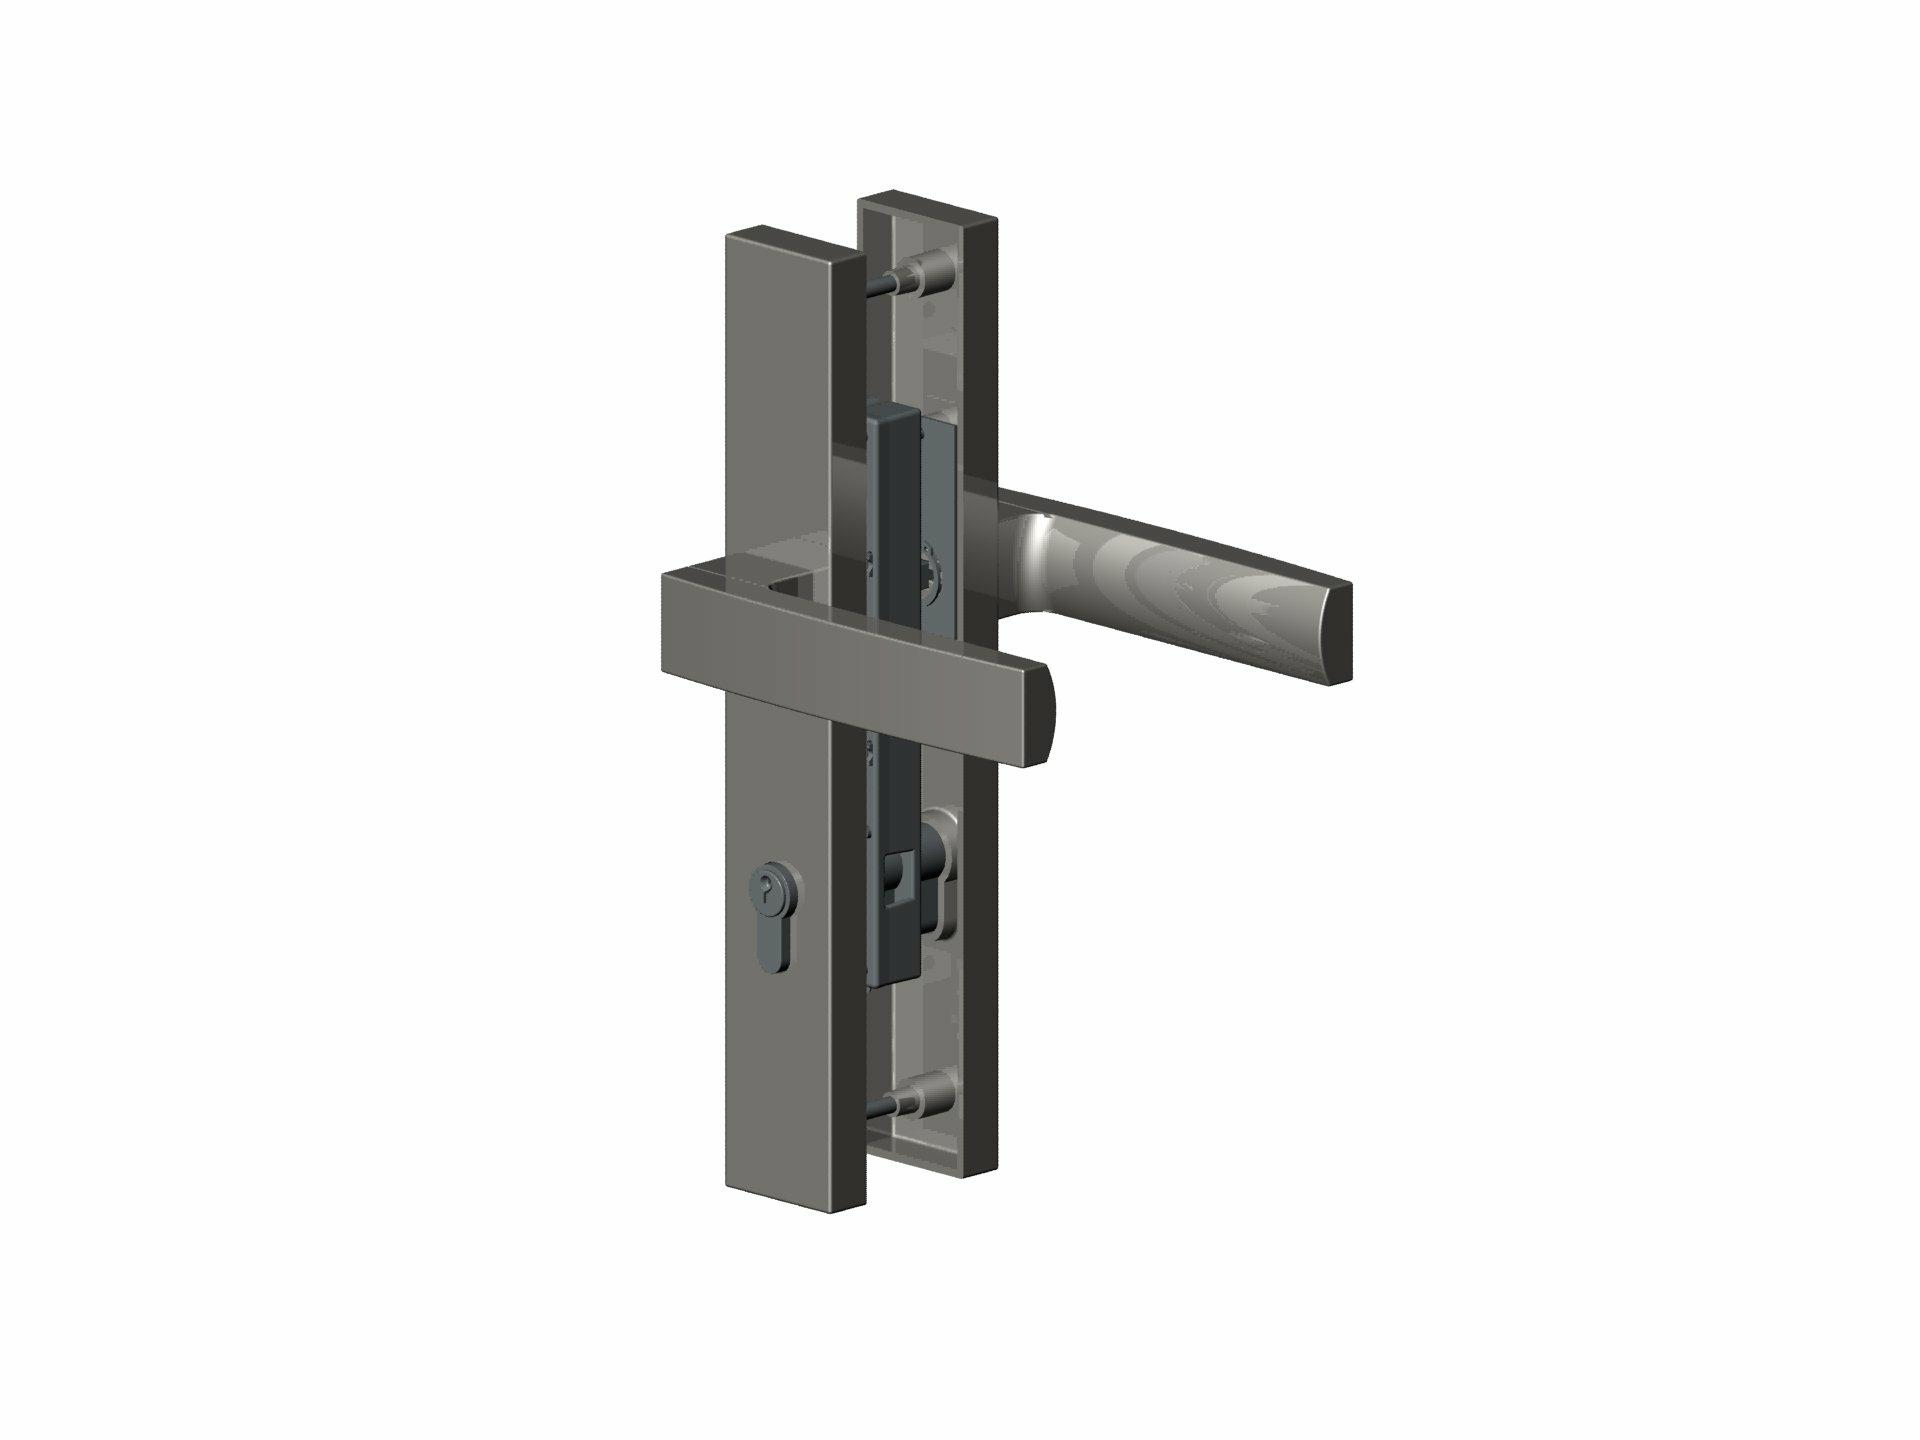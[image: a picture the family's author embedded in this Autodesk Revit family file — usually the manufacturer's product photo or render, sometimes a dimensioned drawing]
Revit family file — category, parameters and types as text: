
# Revit family: APL Magnum 50 French Door
name_source: partatom
category: Doors
revit_build: Autodesk Revit LT 2018 (Build: 20170223_1515(x64)
units: mm (PartAtom-declared; Revit-internal decimal feet)

## family parameters
Always vertical = Yes
Cut with Voids When Loaded = No
Host = Wall
OmniClass Number = 23.30.10.00
OmniClass Title = Doors
Room Calculation Point = No
Shared = No

## types (2) — shared parameters
15° Opening = Yes
90° Opening = No
Analytic Construction = <None>
Architrave = Yes
Frame Projection Ext. = 13 mm
Frame Projection Int. = 20 mm  [stored 0.0656168 ft]
Frame Width = 13 mm
Frame Width Sill = 15 mm  [stored 0.0492126 ft]
Function = Interior
Groove = 10 mm  [stored 0.0328084 ft]
Handle External Left = Yes
Handle External Right = Yes
Handle Internal Left = Yes
Handle Internal Right = Yes
Height = 2201 mm
Jamb Liner 1 = Yes
Jamb Liner 2 = Yes
Left Handle = No
Liner End = 10 mm  [stored 0.0328084 ft]
Liner Head = Yes
Liner Sill = No
Lock External Left = Yes
Lock External Right = Yes
Lock Internal Left = Yes
Lock Internal Right = Yes
Opening Annotation = Yes
Reveal Liner = No
Right Handle = Yes
Rough Height = 2213 mm
Rough Width = 1615 mm  [stored 5.29856 ft]
Wall Closure = By host
Width = 1600 mm  [stored 5.24934 ft]
zero-valued in all types: Thickness

## type names (no varying parameters)
- Architrave
- Liner

note: [stored X ft] marks values corroborated as IEEE doubles in the binary element streams (Revit-internal decimal feet)

## geometry (parser evidence)
native form markers: Extrusion x7, Sweep x31
no freeform markers — native parametric forms only
